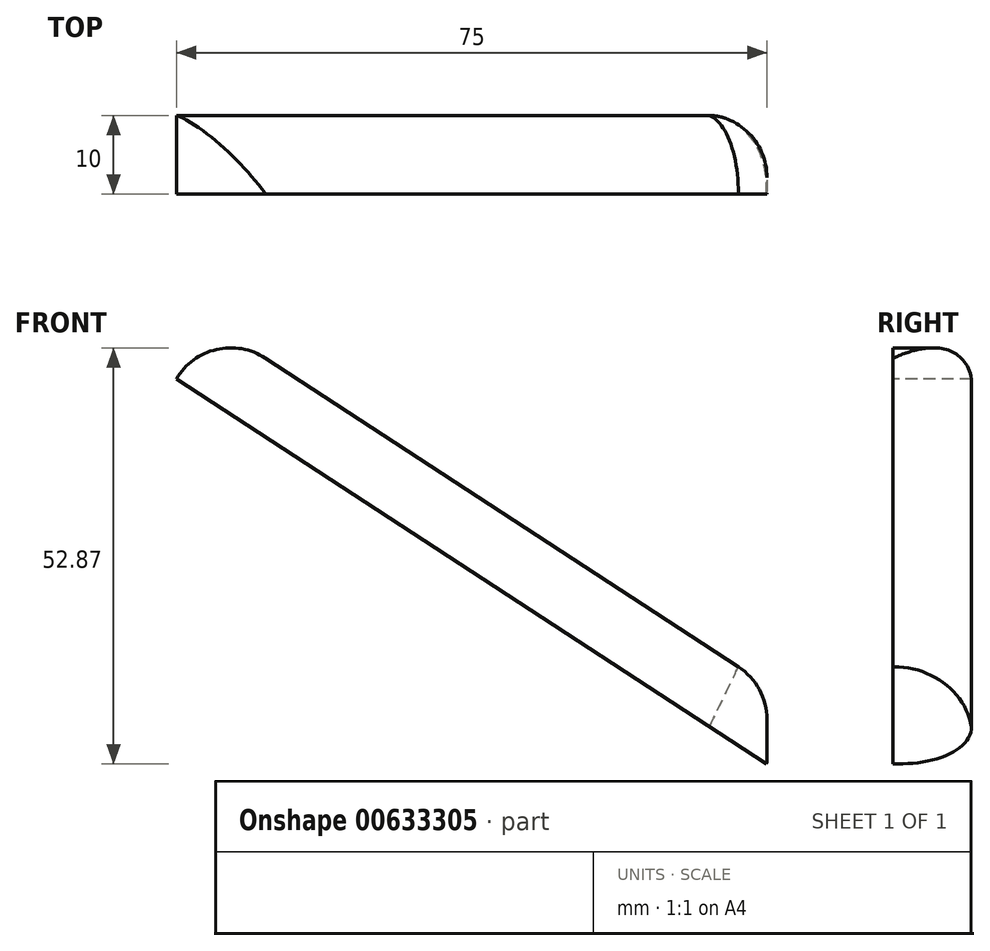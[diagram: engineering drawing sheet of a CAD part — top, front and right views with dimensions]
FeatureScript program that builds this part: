
annotation { "Feature Type Name" : "Feature", "Feature Type Description" : "" }
export const myFeature = defineFeature(function(context is Context, id is Id, definition is map)
    precondition{}
    {
        {
            var Q0;
            Q0=qCreatedBy(makeId("Front.planeOp"),FACE);
            var sketch = newSketch(context, id + "F0", { "sketchPlane" : qUnion([Q0])});
            skLineSegment(sketch, "E0", {"start": v(-37.5, 58.78) * mm, "end": v(-37.5, -69.07) * mm, "construction": true});
            skLineSegment(sketch, "E1", {"start": v(37.5, 60.72) * mm, "end": v(37.5, -69.85) * mm, "construction": true});
            skLineSegment(sketch, "E2", {"start": v(-37.5, 21.12) * mm, "end": v(37.5, -27.83) * mm});
            skLineSegment(sketch, "E3", {"start": v(37.5, -27.83) * mm, "end": v(37.5, -37.83) * mm});
            skLineSegment(sketch, "E4", {"start": v(37.5, -37.83) * mm, "end": v(-37.5, 11.12) * mm});
            skLineSegment(sketch, "E5", {"start": v(-37.5, 11.12) * mm, "end": v(-37.5, 21.12) * mm});
            skSolve(sketch);
        }
        {
            var Q0;
            Q0=qSketchRegion(id+"F0",true);
            extrude(context, id + "F1", {"entities" : qUnion([Q0]), "depth" : 10 * mm, "offsetDistance" : 25 * mm});
        }
        {
            var Q0;
            Q0=makeQuery(id+"F1.opExtrude","CAP_EDGE",EDGE,{"disambiguationData":[OSD([sQuery(id+"F0.wireOp",EDGE,"E2")])],"isStart":false});
            fillet(context, id + "F2", {"entities" : qUnion([Q0]), "radius" : 10 * mm, "tangentPropagation" : true, "allowEdgeOverflow" : false});
        }
        {
            var Q0;
            Q0=makeQuery(id+"F2.opFillet","BLEND_EDGE",EDGE,{"blendedFrom":[makeQuery(id+"F1.opExtrude","CAP_EDGE",EDGE,{"disambiguationData":[OSD([sQuery(id+"F0.wireOp",EDGE,"E2")])],"isStart":false}),makeQuery(id+"F1.opExtrude","SWEPT_FACE",FACE,{"disambiguationData":[OSD([sQuery(id+"F0.wireOp",EDGE,"E3")])]})],"blendedInto":[makeQuery(id+"F1.opExtrude","SWEPT_FACE",FACE,{"disambiguationData":[OSD([sQuery(id+"F0.wireOp",EDGE,"E3")])]})]});
            var Q1;
            Q1=makeQuery(id+"F2.opFillet","BLEND_EDGE",EDGE,{"blendedFrom":[makeQuery(id+"F1.opExtrude","CAP_EDGE",EDGE,{"disambiguationData":[OSD([sQuery(id+"F0.wireOp",EDGE,"E2")])],"isStart":false}),makeQuery(id+"F1.opExtrude","SWEPT_FACE",FACE,{"disambiguationData":[OSD([sQuery(id+"F0.wireOp",EDGE,"E5")])]})],"blendedInto":[makeQuery(id+"F1.opExtrude","SWEPT_FACE",FACE,{"disambiguationData":[OSD([sQuery(id+"F0.wireOp",EDGE,"E5")])]})]});
            fillet(context, id + "F3", {"entities" : qUnion([Q0, Q1]), "radius" : 8 * mm, "tangentPropagation" : true, "allowEdgeOverflow" : false});
        }
        {
            var Q0;
            Q0=makeQuery(id+"F1.opExtrude","SWEPT_BODY",BODY,{"disambiguationData":[OSD([sQuery(id+"F0.wireOp",EDGE,"E2"),sQuery(id+"F0.wireOp",EDGE,"E3"),sQuery(id+"F0.wireOp",EDGE,"E4"),sQuery(id+"F0.wireOp",EDGE,"E5")])]});
            var Q1;
            Q1=qCreatedBy(makeId("Front.planeOp"),FACE);
            mirror(context, id + "F4", {"entities" : qUnion([Q0]), "mirrorPlane" : qUnion([Q1])});
        }
        {
            var Q0;
            Q0=makeQuery(id+"F1.opExtrude","SWEPT_BODY",BODY,{"disambiguationData":[OSD([sQuery(id+"F0.wireOp",EDGE,"E2"),sQuery(id+"F0.wireOp",EDGE,"E3"),sQuery(id+"F0.wireOp",EDGE,"E4"),sQuery(id+"F0.wireOp",EDGE,"E5")])]});
            deleteBodies(context, id + "F5", {"entities" : qUnion([Q0])});
        }
    });
